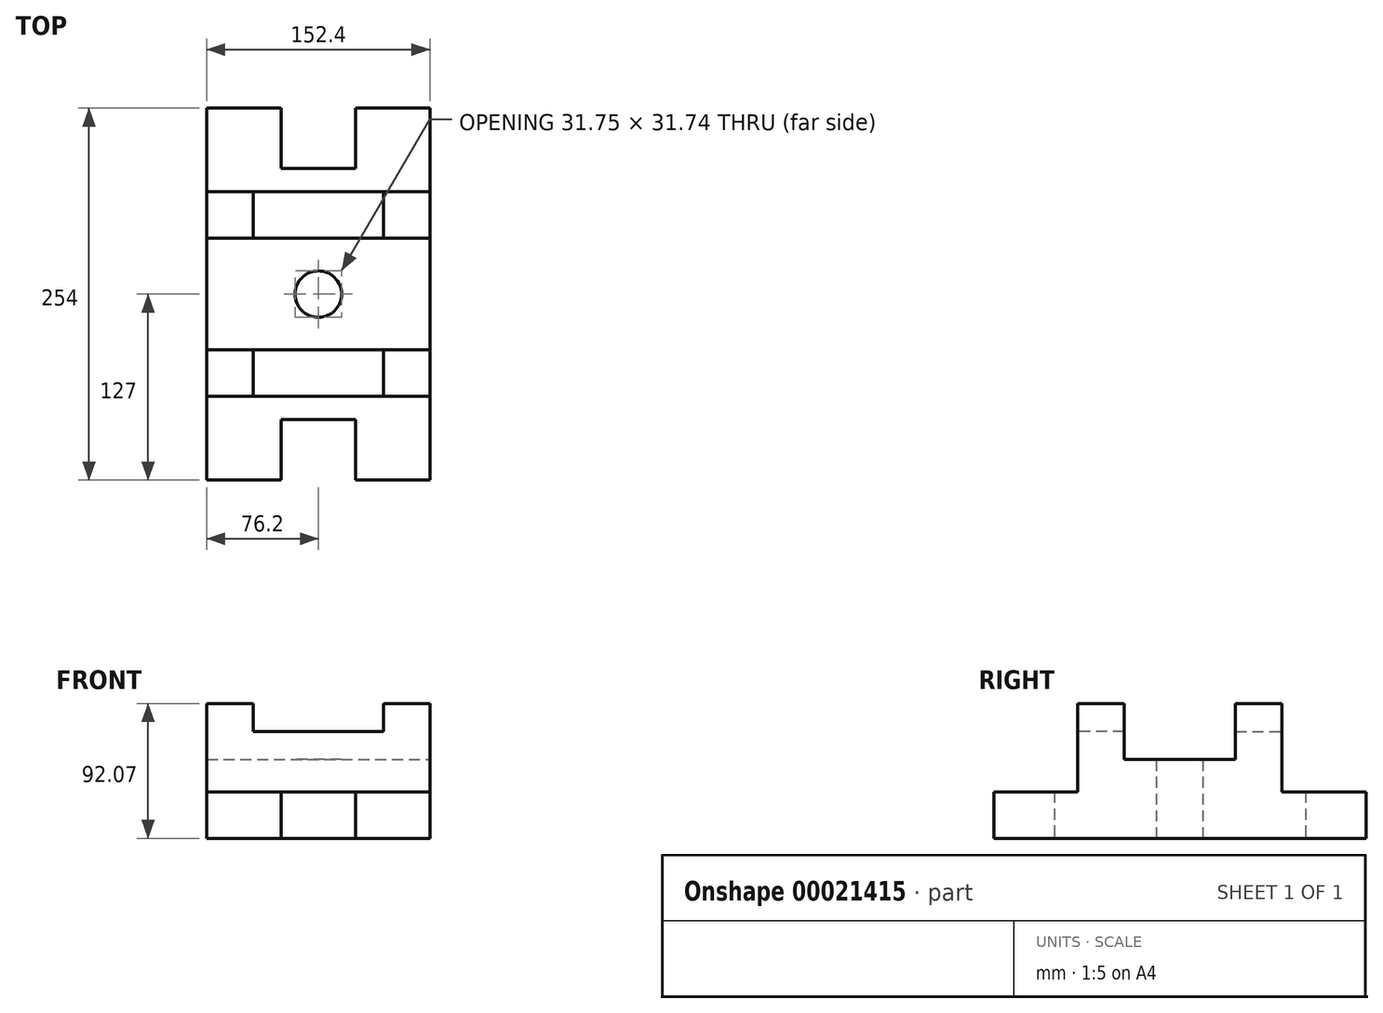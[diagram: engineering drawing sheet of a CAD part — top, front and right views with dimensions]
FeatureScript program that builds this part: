
annotation { "Feature Type Name" : "Feature", "Feature Type Description" : "" }
export const myFeature = defineFeature(function(context is Context, id is Id, definition is map)
    precondition{}
    {
        {
            var Q0;
            Q0=qCreatedBy(makeId("Front.planeOp"),FACE);
            var sketch = newSketch(context, id + "F0", { "sketchPlane" : qUnion([Q0])});
            skLineSegment(sketch, "E0.bottom", {"start": v(-82.7, 62.15) * mm, "end": v(69.7, 62.15) * mm});
            skLineSegment(sketch, "E0.top", {"start": v(-82.7, -29.92) * mm, "end": v(69.7, -29.92) * mm});
            skLineSegment(sketch, "E0.left", {"start": v(-82.7, 62.15) * mm, "end": v(-82.7, -29.92) * mm});
            skLineSegment(sketch, "E0.right", {"start": v(69.7, 62.15) * mm, "end": v(69.7, -29.92) * mm});
            skLineSegment(sketch, "E1", {"start": v(-50.95, 62.15) * mm, "end": v(-50.95, 43.1) * mm});
            skLineSegment(sketch, "E2", {"start": v(37.95, 62.15) * mm, "end": v(37.95, 43.1) * mm});
            skLineSegment(sketch, "E3", {"start": v(-50.95, 43.1) * mm, "end": v(37.95, 43.1) * mm});
            skLineSegment(sketch, "E4", {"start": v(-31.9, 1.83) * mm, "end": v(-31.9, -29.92) * mm});
            skLineSegment(sketch, "E5", {"start": v(18.9, 1.83) * mm, "end": v(18.9, -29.92) * mm});
            skLineSegment(sketch, "E6", {"start": v(-31.9, 1.83) * mm, "end": v(18.9, 1.83) * mm});
            skLineSegment(sketch, "E7.top", {"start": v(-31.9, -29.92) * mm, "end": v(18.9, -29.92) * mm});
            skSolve(sketch);
        }
        {
            var Q0;
            Q0 = qSketchRegion(id + "F0", true);
            extrude(context, id + "F1", {"entities" : qUnion([Q0]), "depth" : 127 * mm});
        }
        {
            var Q0;
            {var subQ1=sQuery(id+"F0.wireOp",EDGE,"E1");Q0=makeQuery(id+"F0.imprint","IMPRINT",FACE,{"disambiguationData":[TD([[makeQuery(id+"F0.imprint","IMPRINT",EDGE,{"derivedFrom":subQ1}),1.0]])]});}
            extrude(context, id + "F2", {"entities" : qUnion([Q0]), "operationType" : NewBodyOperationType.REMOVE, "depth" : 31.75 * mm});
        }
        {
            var Q0;
            Q0=makeQuery(id+"F0.imprint","IMPRINT",FACE,{"disambiguationData":[TD([[makeQuery(id+"F0.imprint","IMPRINT",EDGE,{"derivedFrom":sQuery(id+"F0.wireOp",EDGE,"E6")}),-1.0]])]});
            extrude(context, id + "F3", {"entities" : qUnion([Q0]), "operationType" : NewBodyOperationType.REMOVE, "depth" : 41.27 * mm});
        }
        {
            var Q0;
            Q0=makeQuery(id+"F1.opExtrude","SWEPT_FACE",FACE,{"disambiguationData":[OSD([sQuery(id+"F0.wireOp",EDGE,"E0.right")])]});
            var sketch = newSketch(context, id + "F4", { "sketchPlane" : qUnion([Q0])});
            skLineSegment(sketch, "E8", {"start": v(-57.15, 62.15) * mm, "end": v(-57.15, 1.83) * mm});
            skLineSegment(sketch, "E9", {"start": v(-57.15, 1.83) * mm, "end": v(0, 1.83) * mm});
            skLineSegment(sketch, "E10", {"start": v(-88.9, 62.15) * mm, "end": v(-88.9, 24.05) * mm});
            skLineSegment(sketch, "E11", {"start": v(-88.9, 24.05) * mm, "end": v(-127, 24.05) * mm});
            skSolve(sketch);
        }
        {
            var Q0;
            {var subQ5=sQuery(id+"F4.wireOp",EDGE,"E8");Q0=makeQuery(id+"F4.imprint","IMPRINT",FACE,{"disambiguationData":[TD([[makeQuery(id+"F4.imprint","IMPRINT",EDGE,{"derivedFrom":subQ5}),1.0]])]});}
            extrude(context, id + "F5", {"entities" : qUnion([Q0]), "operationType" : NewBodyOperationType.REMOVE, "oppositeDirection" : true, "depth" : 152.4 * mm});
        }
        {
            var Q0;
            Q0=makeQuery(id+"F5.boolean.opBoolean","COPY",FACE,{"derivedFrom":makeQuery(id+"F5.opExtrude","SWEPT_FACE",FACE,{"disambiguationData":[OSD([sQuery(id+"F4.wireOp",EDGE,"E8")])]})});
            var sketch = newSketch(context, id + "F6", { "sketchPlane" : qUnion([Q0])});
            skLineSegment(sketch, "E12", {"start": v(-37.95, 62.15) * mm, "end": v(-37.95, 43.1) * mm});
            skLineSegment(sketch, "E13", {"start": v(50.95, 62.15) * mm, "end": v(50.95, 43.1) * mm});
            skLineSegment(sketch, "E14", {"start": v(-37.95, 43.1) * mm, "end": v(50.95, 43.1) * mm});
            skSolve(sketch);
        }
        {
            var Q0;
            {var subQ2=sQuery(id+"F6.wireOp",EDGE,"E12");Q0=makeQuery(id+"F6.imprint","IMPRINT",FACE,{"disambiguationData":[TD([[makeQuery(id+"F6.imprint","IMPRINT",EDGE,{"derivedFrom":subQ2}),1.0]])]});}
            extrude(context, id + "F7", {"entities" : qUnion([Q0]), "operationType" : NewBodyOperationType.REMOVE, "oppositeDirection" : true, "depth" : 31.75 * mm});
        }
        {
            var Q0;
            {var subQ5=sQuery(id+"F4.wireOp",EDGE,"E10");Q0=makeQuery(id+"F4.imprint","IMPRINT",FACE,{"disambiguationData":[TD([[makeQuery(id+"F4.imprint","IMPRINT",EDGE,{"derivedFrom":subQ5}),-1.0]])]});}
            extrude(context, id + "F8", {"entities" : qUnion([Q0]), "operationType" : NewBodyOperationType.REMOVE, "oppositeDirection" : true, "depth" : 152.4 * mm});
        }
        {
            var Q0;
            Q0=makeQuery(id+"F8.boolean.opBoolean","COPY",FACE,{"derivedFrom":makeQuery(id+"F8.opExtrude","SWEPT_FACE",FACE,{"disambiguationData":[OSD([sQuery(id+"F4.wireOp",EDGE,"E11")])]})});
            var sketch = newSketch(context, id + "F9", { "sketchPlane" : qUnion([Q0])});
            skArc(sketch, "E15", {"start": v(9.35, -127.87) * mm, "mid": v(-6.24, -111.13) * mm, "end": v(-22.37, -127.35) * mm});
            skLineSegment(sketch, "E16", {"start": v(9.35, -127.87) * mm, "end": v(9.35, -127.87) * mm});
            skSolve(sketch);
        }
        {
            var Q0;
            {var subQ0=makeQuery(id+"F8.boolean.opBoolean","COPY",EDGE,{"derivedFrom":makeQuery(id+"F8.opExtrude","SWEPT_EDGE",EDGE,{"disambiguationData":[OSD([sQuery(id+"F0.wireOp",EDGE,"E0.right"),sQuery(id+"F4.wireOp",EDGE,"E11")])]})});var subQ1=sQuery(id+"F9.wireOp",EDGE,"E15");var subQ3=makeQuery(id+"F9.imprint","INTERSECT",VERTEX,{"disambiguationData":[OD(0.0)],"derivedFrom":[subQ0,subQ1]});Q0=makeQuery(id+"F9.imprint","IMPRINT",FACE,{"disambiguationData":[TD([[makeQuery(id+"F9.imprint","IMPRINT",EDGE,{"disambiguationData":[TD([[subQ3,-1.0]])],"derivedFrom":subQ1}),1.0]])]});}
            extrude(context, id + "F10", {"entities" : qUnion([Q0]), "operationType" : NewBodyOperationType.REMOVE, "oppositeDirection" : true, "depth" : 53.97 * mm});
        }
        {
            var Q0;
            Q0=makeQuery(id+"F1.opExtrude","SWEPT_BODY",BODY,{"disambiguationData":[OSD([sQuery(id+"F0.wireOp",EDGE,"E0.bottom"),sQuery(id+"F0.wireOp",EDGE,"E0.top"),sQuery(id+"F0.wireOp",EDGE,"E0.left"),sQuery(id+"F0.wireOp",EDGE,"E0.right"),sQuery(id+"F0.wireOp",EDGE,"E7.top")])]});
            var Q1;
            {var subQ0=sQuery(id+"F0.wireOp",EDGE,"E0.top");var subQ1=sQuery(id+"F0.wireOp",EDGE,"E0.left");var subQ2=sQuery(id+"F0.wireOp",EDGE,"E7.top");Q1=makeQuery(id+"F10.boolean.opBoolean","SPLIT",FACE,{"disambiguationData":[TD([makeQuery(id+"F1.opExtrude","SWEPT_FACE",FACE,{"disambiguationData":[OSD([subQ1])]})])],"derivedFrom":makeQuery(id+"F1.opExtrude","CAP_FACE",FACE,{"disambiguationData":[OSD([sQuery(id+"F0.wireOp",EDGE,"E0.bottom"),subQ0,subQ1,sQuery(id+"F0.wireOp",EDGE,"E0.right"),subQ2])],"isStart":false})});}
            mirror(context, id + "F11", {"operationType" : NewBodyOperationType.ADD, "entities" : qUnion([Q0]), "mirrorPlane" : qUnion([Q1])});
        }
    });
